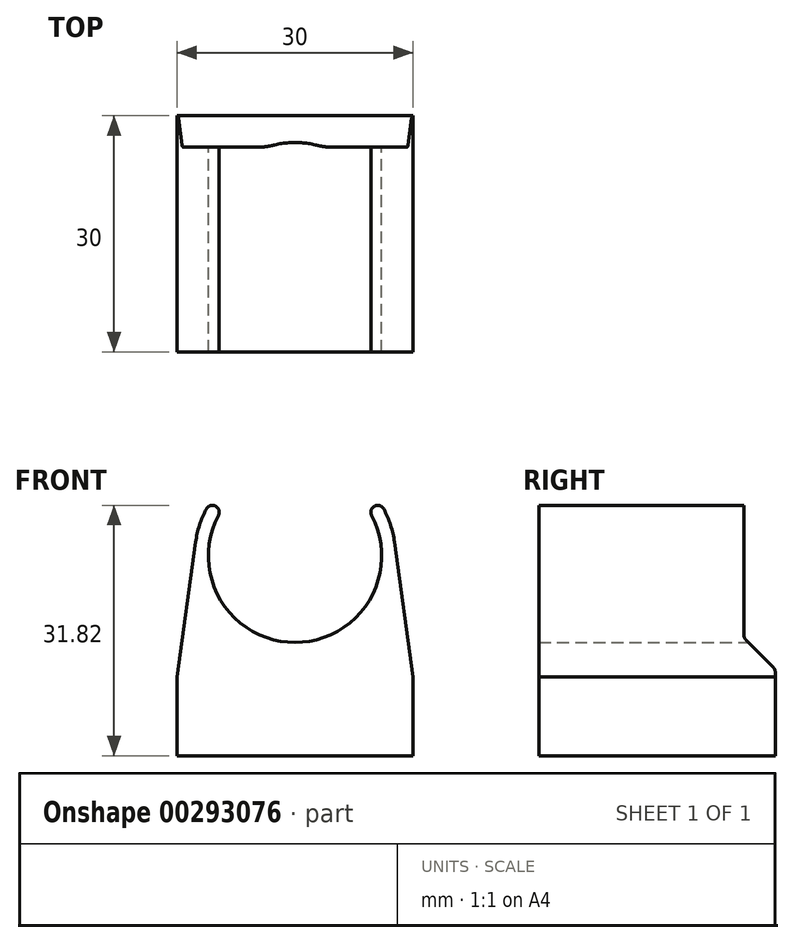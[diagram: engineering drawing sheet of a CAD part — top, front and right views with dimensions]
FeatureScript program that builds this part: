
annotation { "Feature Type Name" : "Feature", "Feature Type Description" : "" }
export const myFeature = defineFeature(function(context is Context, id is Id, definition is map)
    precondition{}
    {
        {
            var Q0;
            Q0=qCreatedBy(makeId("Front.planeOp"),FACE);
            var sketch = newSketch(context, id + "F0", { "sketchPlane" : qUnion([Q0])});
            skLineSegment(sketch, "E0.bottom", {"start": v(-15, 0) * mm, "end": v(15, 0) * mm});
            skLineSegment(sketch, "E0.top", {"start": v(-15, 10) * mm, "end": v(15, 10) * mm, "construction": true});
            skLineSegment(sketch, "E0.left", {"start": v(-15, 0) * mm, "end": v(-15, 10) * mm});
            skLineSegment(sketch, "E0.right", {"start": v(15, 0) * mm, "end": v(15, 10) * mm});
            skLineSegment(sketch, "E1", {"start": v(0, 10) * mm, "end": v(0, 14.4) * mm, "construction": true});
            skPoint(sketch, "E1.endSnap0", {"position": v(0, 10) * mm});
            skArc(sketch, "E2", {"start": v(-9.73, 30.54) * mm, "mid": v(0, 14.4) * mm, "end": v(9.73, 30.54) * mm});
            skArc(sketch, "E3", {"start": v(12.63, 27.15) * mm, "mid": v(12.14, 29.3) * mm, "end": v(11.27, 31.36) * mm});
            skLineSegment(sketch, "E4", {"start": v(-15, 10) * mm, "end": v(-12.63, 27.15) * mm});
            skLineSegment(sketch, "E5", {"start": v(15, 10) * mm, "end": v(12.63, 27.15) * mm});
            skArc(sketch, "E6", {"start": v(-9.73, 30.54) * mm, "mid": v(-10.1, 31.72) * mm, "end": v(-11.27, 31.36) * mm});
            skArc(sketch, "E7", {"start": v(11.27, 31.36) * mm, "mid": v(10.1, 31.72) * mm, "end": v(9.73, 30.54) * mm});
            skLineSegment(sketch, "E8", {"start": v(-9.63, 35.6) * mm, "end": v(-9.63, 27.49) * mm, "construction": true});
            skLineSegment(sketch, "E9", {"start": v(9.62, 38.1) * mm, "end": v(9.62, 26.4) * mm, "construction": true});
            skArc(sketch, "E10.trimOffspring", {"start": v(-11.27, 31.36) * mm, "mid": v(-12.14, 29.3) * mm, "end": v(-12.63, 27.15) * mm});
            skSolve(sketch);
        }
        {
            var Q0;
            Q0=qSketchRegion(id+"F0",true);
            extrude(context, id + "F1", {"entities" : qUnion([Q0]), "depth" : 26 * mm});
        }
        {
            var Q0;
            Q0=makeQuery(id+"F1.opExtrude","CAP_FACE",FACE,{"disambiguationData":[OSD([sQuery(id+"F0.wireOp",EDGE,"E0.bottom"),sQuery(id+"F0.wireOp",EDGE,"E0.left"),sQuery(id+"F0.wireOp",EDGE,"E0.right"),sQuery(id+"F0.wireOp",EDGE,"E2"),sQuery(id+"F0.wireOp",EDGE,"E3"),sQuery(id+"F0.wireOp",EDGE,"E4"),sQuery(id+"F0.wireOp",EDGE,"E5"),sQuery(id+"F0.wireOp",EDGE,"E6"),sQuery(id+"F0.wireOp",EDGE,"E7"),sQuery(id+"F0.wireOp",EDGE,"E10.trimOffspring")])],"isStart":true});
            var sketch = newSketch(context, id + "F2", { "sketchPlane" : qUnion([Q0])});
            skLineSegment(sketch, "E11.0", {"start": v(15, 0) * mm, "end": v(-15, 0) * mm});
            skLineSegment(sketch, "E12.0", {"start": v(15, 0) * mm, "end": v(15, 10) * mm});
            skLineSegment(sketch, "E13.0", {"start": v(15, 10) * mm, "end": v(14.3, 15) * mm});
            skLineSegment(sketch, "E14.0", {"start": v(-15, 10) * mm, "end": v(-14.3, 15) * mm});
            skLineSegment(sketch, "E15.0", {"start": v(-15, 0) * mm, "end": v(-15, 10) * mm});
            skArc(sketch, "E16.0", {"start": v(3.58, 15) * mm, "mid": v(0, 14.4) * mm, "end": v(-3.58, 15) * mm});
            skLineSegment(sketch, "E17", {"start": v(-14.3, 15) * mm, "end": v(-3.58, 15) * mm});
            skPoint(sketch, "E18.orphan", {"position": v(-9.73, 30.54) * mm});
            skPoint(sketch, "E19.orphan", {"position": v(-12.63, 27.15) * mm});
            skLineSegment(sketch, "E20.trimOffspring", {"start": v(3.58, 15) * mm, "end": v(14.3, 15) * mm});
            skPoint(sketch, "E21.orphan", {"position": v(9.73, 30.54) * mm});
            skPoint(sketch, "E22.orphan", {"position": v(12.63, 27.15) * mm});
            skSolve(sketch);
        }
        {
            var Q0;
            Q0=qSketchRegion(id+"F2",true);
            extrude(context, id + "F3", {"entities" : qUnion([Q0]), "operationType" : NewBodyOperationType.ADD, "depth" : 4 * mm});
        }
        {
            var Q0;
            Q0=makeQuery(id+"F3.opExtrude","CAP_EDGE",EDGE,{"disambiguationData":[OSD([sQuery(id+"F2.wireOp",EDGE,"E20.trimOffspring")])],"isStart":false});
            chamfer(context, id + "F4", {"entities" : qUnion([Q0]), "width" : 4 * mm, "tangentPropagation" : true});
        }
        {
            var Q0;
            {var subQ0=sQuery(id+"F0.wireOp",EDGE,"E7");var subQ1=sQuery(id+"F0.wireOp",EDGE,"E5");var subQ2=sQuery(id+"F0.wireOp",EDGE,"E3");var subQ3=sQuery(id+"F0.wireOp",EDGE,"E2");Q0=makeQuery(id+"F4.opChamfer","BLEND_EDGE",EDGE,{"blendedFrom":[makeQuery(id+"F3.opExtrude","CAP_EDGE",EDGE,{"disambiguationData":[OSD([sQuery(id+"F2.wireOp",EDGE,"E20.trimOffspring")])],"isStart":false}),makeQuery(id+"F3.boolean.opBoolean","SPLIT",FACE,{"disambiguationData":[TD([makeQuery(id+"F1.opExtrude","SWEPT_FACE",FACE,{"disambiguationData":[OSD([subQ2])]})])],"derivedFrom":makeQuery(id+"F1.opExtrude","CAP_FACE",FACE,{"disambiguationData":[OSD([sQuery(id+"F0.wireOp",EDGE,"E0.bottom"),sQuery(id+"F0.wireOp",EDGE,"E0.left"),sQuery(id+"F0.wireOp",EDGE,"E0.right"),subQ3,subQ2,sQuery(id+"F0.wireOp",EDGE,"E4"),subQ1,sQuery(id+"F0.wireOp",EDGE,"E6"),subQ0,sQuery(id+"F0.wireOp",EDGE,"E10.trimOffspring")])],"isStart":true})})],"blendedInto":[makeQuery(id+"F3.boolean.opBoolean","SPLIT",FACE,{"disambiguationData":[TD([makeQuery(id+"F1.opExtrude","SWEPT_FACE",FACE,{"disambiguationData":[OSD([subQ2])]})])],"derivedFrom":makeQuery(id+"F1.opExtrude","CAP_FACE",FACE,{"disambiguationData":[OSD([sQuery(id+"F0.wireOp",EDGE,"E0.bottom"),sQuery(id+"F0.wireOp",EDGE,"E0.left"),sQuery(id+"F0.wireOp",EDGE,"E0.right"),subQ3,subQ2,sQuery(id+"F0.wireOp",EDGE,"E4"),subQ1,sQuery(id+"F0.wireOp",EDGE,"E6"),subQ0,sQuery(id+"F0.wireOp",EDGE,"E10.trimOffspring")])],"isStart":true})})]});}
            fillet(context, id + "F5", {"entities" : qUnion([Q0]), "radius" : 1 * mm, "tangentPropagation" : true, "allowEdgeOverflow" : false});
        }
        {
            var Q0;
            {var subQ0=sQuery(id+"F0.wireOp",EDGE,"E10.trimOffspring");var subQ1=sQuery(id+"F0.wireOp",EDGE,"E6");var subQ2=sQuery(id+"F0.wireOp",EDGE,"E4");var subQ3=sQuery(id+"F0.wireOp",EDGE,"E2");var subQ4=sQuery(id+"F2.wireOp",EDGE,"E20.trimOffspring");Q0=makeQuery(id+"F4.opChamfer","BLEND_EDGE",EDGE,{"blendedFrom":[makeQuery(id+"F3.opExtrude","CAP_EDGE",EDGE,{"disambiguationData":[OSD([subQ4])],"isStart":false}),makeQuery(id+"F3.boolean.opBoolean","SPLIT",FACE,{"disambiguationData":[TD([makeQuery(id+"F1.opExtrude","SWEPT_FACE",FACE,{"disambiguationData":[OSD([subQ2])]})])],"derivedFrom":makeQuery(id+"F1.opExtrude","CAP_FACE",FACE,{"disambiguationData":[OSD([sQuery(id+"F0.wireOp",EDGE,"E0.bottom"),sQuery(id+"F0.wireOp",EDGE,"E0.left"),sQuery(id+"F0.wireOp",EDGE,"E0.right"),subQ3,sQuery(id+"F0.wireOp",EDGE,"E3"),subQ2,sQuery(id+"F0.wireOp",EDGE,"E5"),subQ1,sQuery(id+"F0.wireOp",EDGE,"E7"),subQ0])],"isStart":true})})],"blendedInto":[makeQuery(id+"F3.boolean.opBoolean","SPLIT",FACE,{"disambiguationData":[TD([makeQuery(id+"F1.opExtrude","SWEPT_FACE",FACE,{"disambiguationData":[OSD([subQ2])]})])],"derivedFrom":makeQuery(id+"F1.opExtrude","CAP_FACE",FACE,{"disambiguationData":[OSD([sQuery(id+"F0.wireOp",EDGE,"E0.bottom"),sQuery(id+"F0.wireOp",EDGE,"E0.left"),sQuery(id+"F0.wireOp",EDGE,"E0.right"),subQ3,sQuery(id+"F0.wireOp",EDGE,"E3"),subQ2,sQuery(id+"F0.wireOp",EDGE,"E5"),subQ1,sQuery(id+"F0.wireOp",EDGE,"E7"),subQ0])],"isStart":true})})]});}
            fillet(context, id + "F6", {"entities" : qUnion([Q0]), "radius" : 1 * mm, "tangentPropagation" : true, "allowEdgeOverflow" : false});
        }
        {
            var Q0;
            {var subQ0=sQuery(id+"F2.wireOp",EDGE,"E20.trimOffspring");Q0=makeQuery(id+"F4.opChamfer","BLEND_EDGE",EDGE,{"blendedFrom":[makeQuery(id+"F3.opExtrude","CAP_EDGE",EDGE,{"disambiguationData":[OSD([subQ0])],"isStart":false}),makeQuery(id+"F3.opExtrude","CAP_FACE",FACE,{"disambiguationData":[OSD([sQuery(id+"F2.wireOp",EDGE,"E11.0"),sQuery(id+"F2.wireOp",EDGE,"E12.0"),sQuery(id+"F2.wireOp",EDGE,"E13.0"),sQuery(id+"F2.wireOp",EDGE,"E14.0"),sQuery(id+"F2.wireOp",EDGE,"E15.0"),sQuery(id+"F2.wireOp",EDGE,"E16.0"),sQuery(id+"F2.wireOp",EDGE,"E17"),subQ0])],"isStart":false})],"blendedInto":[makeQuery(id+"F3.opExtrude","CAP_FACE",FACE,{"disambiguationData":[OSD([sQuery(id+"F2.wireOp",EDGE,"E11.0"),sQuery(id+"F2.wireOp",EDGE,"E12.0"),sQuery(id+"F2.wireOp",EDGE,"E13.0"),sQuery(id+"F2.wireOp",EDGE,"E14.0"),sQuery(id+"F2.wireOp",EDGE,"E15.0"),sQuery(id+"F2.wireOp",EDGE,"E16.0"),sQuery(id+"F2.wireOp",EDGE,"E17"),subQ0])],"isStart":false})]});}
            fillet(context, id + "F7", {"entities" : qUnion([Q0]), "radius" : 1 * mm, "tangentPropagation" : true, "allowEdgeOverflow" : false});
        }
    });
